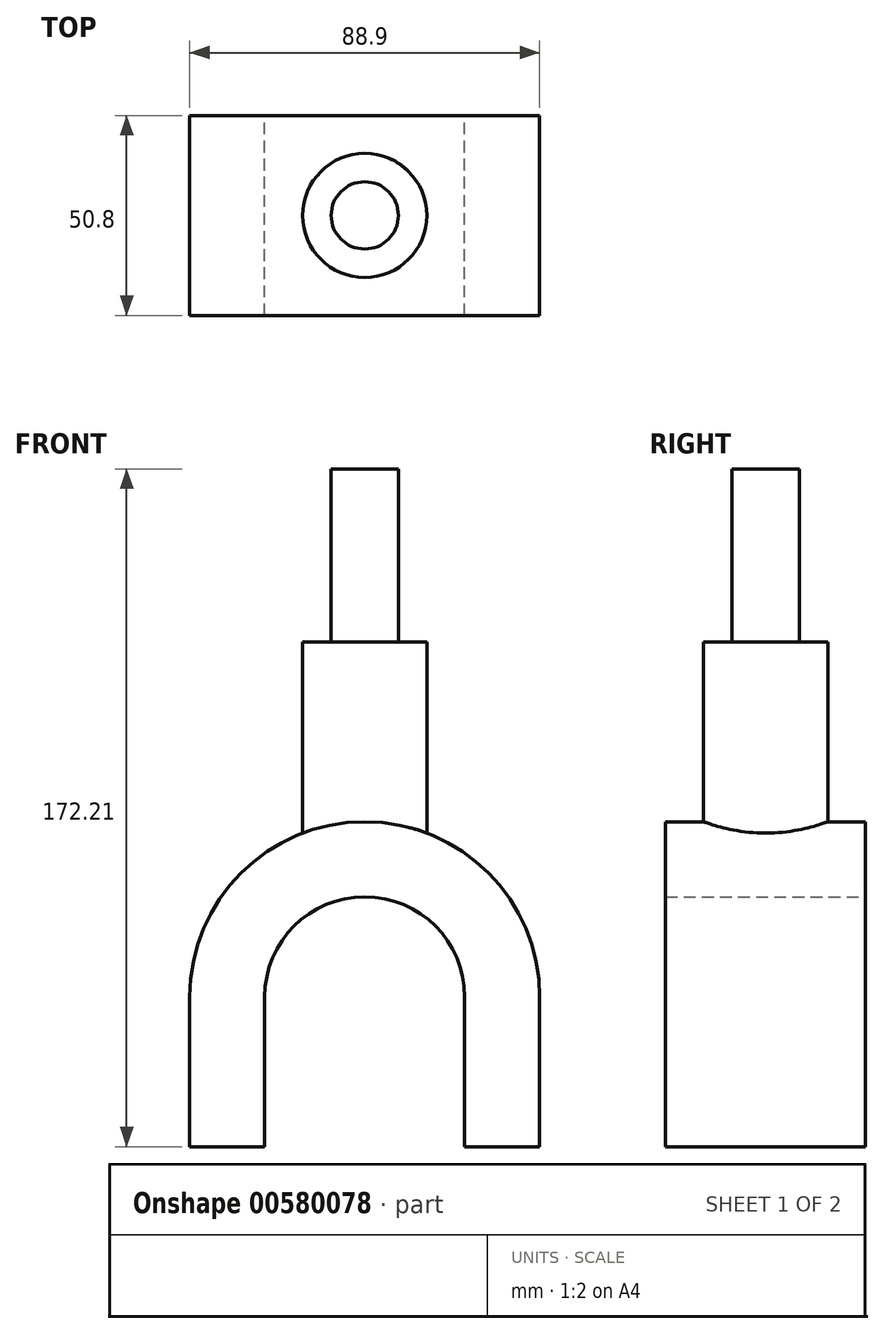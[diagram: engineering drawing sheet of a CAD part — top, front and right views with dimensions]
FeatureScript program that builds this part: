
annotation { "Feature Type Name" : "Feature", "Feature Type Description" : "" }
export const myFeature = defineFeature(function(context is Context, id is Id, definition is map)
    precondition{}
    {
        {
            var Q0;
            Q0=qCreatedBy(makeId("Front.planeOp"),FACE);
            var sketch = newSketch(context, id + "F0", { "sketchPlane" : qUnion([Q0])});
            skArc(sketch, "E0", {"start": v(25.4, 0) * mm, "mid": v(0, 25.4) * mm, "end": v(-25.4, 0) * mm});
            skLineSegment(sketch, "E1", {"start": v(-25.4, 0) * mm, "end": v(-25.4, -38.1) * mm});
            skLineSegment(sketch, "E2", {"start": v(25.4, 0) * mm, "end": v(25.4, -38.1) * mm});
            skLineSegment(sketch, "E3.0", {"start": v(44.45, 0) * mm, "end": v(44.45, -38.1) * mm});
            skLineSegment(sketch, "E4.0", {"start": v(-44.45, 0) * mm, "end": v(-44.45, -38.1) * mm});
            skArc(sketch, "E5.0", {"start": v(44.45, 0) * mm, "mid": v(0, 44.45) * mm, "end": v(-44.45, 0) * mm});
            skLineSegment(sketch, "E6", {"start": v(-44.45, -38.1) * mm, "end": v(-25.4, -38.1) * mm});
            skLineSegment(sketch, "E7", {"start": v(25.4, -38.1) * mm, "end": v(44.45, -38.1) * mm});
            skSolve(sketch);
        }
        {
            var Q0;
            Q0=makeQuery(id+"F0.imprint","IMPRINT",FACE,{"disambiguationData":[TD([[makeQuery(id+"F0.imprint","IMPRINT",EDGE,{"derivedFrom":sQuery(id+"F0.wireOp",EDGE,"E0")}),-1.0]])]});
            extrude(context, id + "F1", {"entities" : qUnion([Q0]), "endBound" : BoundingType.SYMMETRIC, "depth" : 50.8 * mm, "offsetDistance" : 25.4 * mm});
        }
        {
            var Q0;
            Q0=qCreatedBy(makeId("Top.planeOp"),FACE);
            cPlane(context, id + "F2", {"entities" : qUnion([Q0]), "cplaneType" : CPlaneType.OFFSET, "offset" : 90.17 * mm, "width" : 152.4 * mm, "height" : 152.4 * mm});
        }
        {
            var Q0;
            Q0=qCreatedBy(id+"F2.planeOp",FACE);
            var sketch = newSketch(context, id + "F3", { "sketchPlane" : qUnion([Q0])});
            skCircle(sketch, "E8", {"center": v(0, 0) * mm, "radius": 15.77 * mm});
            skSolve(sketch);
        }
        {
            var Q0;
            Q0=makeQuery(id+"F3.imprint","IMPRINT",FACE,{"disambiguationData":[TD([[makeQuery(id+"F3.imprint","IMPRINT",EDGE,{"derivedFrom":sQuery(id+"F3.wireOp",EDGE,"E8")}),1.0]])]});
            var Q1;
            Q1=makeQuery(id+"F1.opExtrude","SWEPT_FACE",FACE,{"disambiguationData":[OSD([sQuery(id+"F0.wireOp",EDGE,"E5.0")])]});
            extrude(context, id + "F4", {"entities" : qUnion([Q0]), "operationType" : NewBodyOperationType.ADD, "endBound" : BoundingType.UP_TO_SURFACE, "oppositeDirection" : true, "depth" : 47.75 * mm, "endBoundEntityFace" : qUnion([Q1]), "offsetDistance" : 25.4 * mm});
        }
        {
            var Q0;
            Q0=qCreatedBy(id+"F2.planeOp",FACE);
            var sketch = newSketch(context, id + "F5", { "sketchPlane" : qUnion([Q0])});
            skCircle(sketch, "E9", {"center": v(0, 0) * mm, "radius": 8.55 * mm});
            skSolve(sketch);
        }
        {
            var Q0;
            Q0=makeQuery(id+"F5.imprint","IMPRINT",FACE,{"disambiguationData":[TD([[makeQuery(id+"F5.imprint","IMPRINT",EDGE,{"derivedFrom":sQuery(id+"F5.wireOp",EDGE,"E9")}),1.0]])]});
            extrude(context, id + "F6", {"entities" : qUnion([Q0]), "operationType" : NewBodyOperationType.ADD, "endBound" : BoundingType.SYMMETRIC, "oppositeDirection" : true, "depth" : 87.88 * mm, "offsetDistance" : 25.4 * mm});
        }
    });
